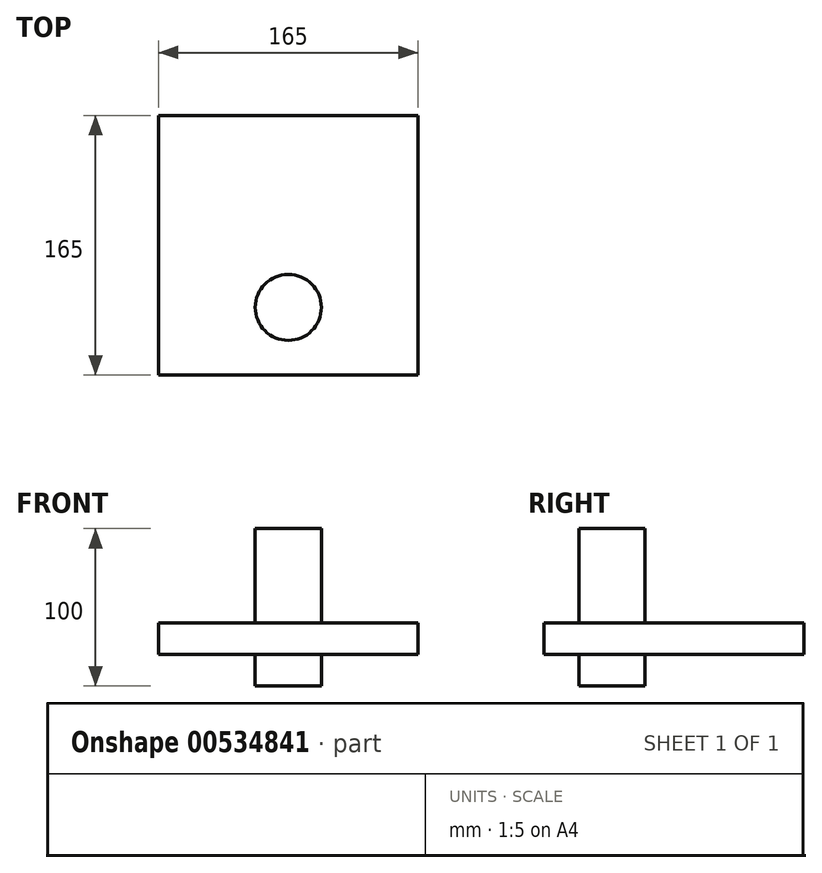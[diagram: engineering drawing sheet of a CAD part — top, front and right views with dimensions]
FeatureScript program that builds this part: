
annotation { "Feature Type Name" : "Feature", "Feature Type Description" : "" }
export const myFeature = defineFeature(function(context is Context, id is Id, definition is map)
    precondition{}
    {
        {
            var Q0;
            Q0=qCreatedBy(makeId("Top.planeOp"),FACE);
            var sketch = newSketch(context, id + "F0", { "sketchPlane" : qUnion([Q0])});
            skLineSegment(sketch, "E0.bottom", {"start": v(82.5, -82.5) * mm, "end": v(-82.5, -82.5) * mm});
            skLineSegment(sketch, "E0.top", {"start": v(82.5, 82.5) * mm, "end": v(-82.5, 82.5) * mm});
            skLineSegment(sketch, "E0.left", {"start": v(82.5, -82.5) * mm, "end": v(82.5, 82.5) * mm});
            skLineSegment(sketch, "E0.right", {"start": v(-82.5, -82.5) * mm, "end": v(-82.5, 82.5) * mm});
            skPoint(sketch, "E0.middle", {"position": v(0, 0) * mm});
            skSolve(sketch);
        }
        {
            var Q0;
            Q0 = qSketchRegion(id + "F0", true);
            extrude(context, id + "F1", {"entities" : qUnion([Q0]), "depth" : 20 * mm, "offsetDistance" : 25 * mm});
        }
        {
            var Q0;
            Q0=qCreatedBy(makeId("Top.planeOp"),FACE);
            var sketch = newSketch(context, id + "F2", { "sketchPlane" : qUnion([Q0])});
            skCircle(sketch, "E1", {"center": v(0, -39.44) * mm, "radius": 21 * mm});
            skSolve(sketch);
        }
        {
            var Q0;
            Q0 = qSketchRegion(id + "F2", true);
            extrude(context, id + "F3", {"entities" : qUnion([Q0]), "operationType" : NewBodyOperationType.ADD, "depth" : 80 * mm, "offsetDistance" : 25 * mm});
        }
        {
            var Q0;
            Q0 = qSketchRegion(id + "F2", true);
            extrude(context, id + "F4", {"entities" : qUnion([Q0]), "operationType" : NewBodyOperationType.ADD, "oppositeDirection" : true, "depth" : 20 * mm, "offsetDistance" : 25 * mm});
        }
    });
